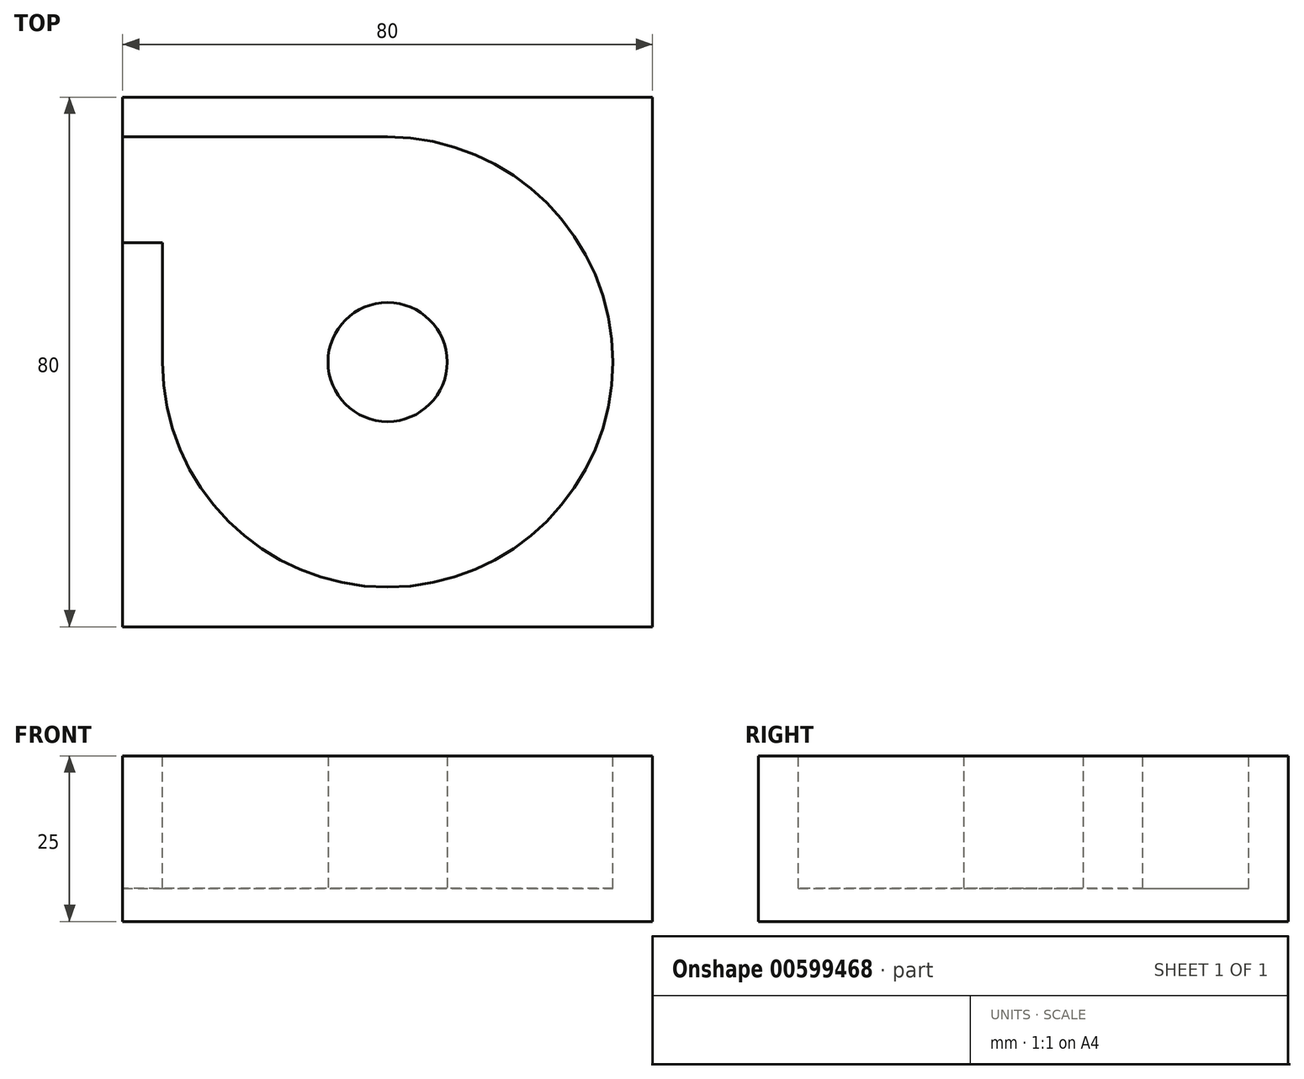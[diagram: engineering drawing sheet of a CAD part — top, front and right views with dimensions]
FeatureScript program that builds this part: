
annotation { "Feature Type Name" : "Feature", "Feature Type Description" : "" }
export const myFeature = defineFeature(function(context is Context, id is Id, definition is map)
    precondition{}
    {
        {
            var Q0;
            Q0=qCreatedBy(makeId("Top.planeOp"),FACE);
            var sketch = newSketch(context, id + "F0", { "sketchPlane" : qUnion([Q0])});
            skLineSegment(sketch, "E0.bottom", {"start": v(-40, 40) * mm, "end": v(40, 40) * mm});
            skLineSegment(sketch, "E0.top", {"start": v(-40, -40) * mm, "end": v(40, -40) * mm});
            skLineSegment(sketch, "E0.left", {"start": v(-40, 40) * mm, "end": v(-40, -40) * mm});
            skLineSegment(sketch, "E0.right", {"start": v(40, 40) * mm, "end": v(40, -40) * mm});
            skPoint(sketch, "E0.middle", {"position": v(0, 0) * mm});
            skSolve(sketch);
        }
        {
            var Q0;
            Q0 = qSketchRegion(id + "F0", true);
            extrude(context, id + "F1", {"entities" : qUnion([Q0]), "depth" : 25 * mm, "offsetDistance" : 25 * mm});
        }
        {
            var Q0;
            Q0=makeQuery(id+"F1.opExtrude","CAP_FACE",FACE,{"disambiguationData":[OSD([sQuery(id+"F0.wireOp",EDGE,"E0.bottom"),sQuery(id+"F0.wireOp",EDGE,"E0.top"),sQuery(id+"F0.wireOp",EDGE,"E0.left"),sQuery(id+"F0.wireOp",EDGE,"E0.right")])],"isStart":false});
            var sketch = newSketch(context, id + "F2", { "sketchPlane" : qUnion([Q0])});
            skCircle(sketch, "E1", {"center": v(0, 0) * mm, "radius": 34 * mm});
            skSolve(sketch);
        }
        {
            var Q0;
            Q0 = qSketchRegion(id + "F2", true);
            extrude(context, id + "F3", {"entities" : qUnion([Q0]), "operationType" : NewBodyOperationType.REMOVE, "oppositeDirection" : true, "depth" : 20 * mm, "offsetDistance" : 25 * mm});
        }
        {
            var Q0;
            Q0=makeQuery(id+"F3.boolean.opBoolean","COPY",FACE,{"derivedFrom":makeQuery(id+"F3.opExtrude","CAP_FACE",FACE,{"disambiguationData":[OSD([sQuery(id+"F2.wireOp",EDGE,"E1")])],"isStart":false})});
            var sketch = newSketch(context, id + "F4", { "sketchPlane" : qUnion([Q0])});
            skCircle(sketch, "E2", {"center": v(0, 0) * mm, "radius": 9 * mm});
            skSolve(sketch);
        }
        {
            var Q0;
            Q0 = qSketchRegion(id + "F4", true);
            extrude(context, id + "F5", {"entities" : qUnion([Q0]), "operationType" : NewBodyOperationType.ADD, "depth" : 20 * mm, "offsetDistance" : 25 * mm});
        }
        {
            var Q0;
            Q0=makeQuery(id+"F1.opExtrude","CAP_FACE",FACE,{"disambiguationData":[OSD([sQuery(id+"F0.wireOp",EDGE,"E0.bottom"),sQuery(id+"F0.wireOp",EDGE,"E0.top"),sQuery(id+"F0.wireOp",EDGE,"E0.left"),sQuery(id+"F0.wireOp",EDGE,"E0.right")])],"isStart":false});
            var sketch = newSketch(context, id + "F6", { "sketchPlane" : qUnion([Q0])});
            skLineSegment(sketch, "E3.bottom", {"start": v(-34, 0) * mm, "end": v(0, 0) * mm});
            skLineSegment(sketch, "E3.top", {"start": v(-34, 34) * mm, "end": v(0, 34) * mm});
            skLineSegment(sketch, "E3.left", {"start": v(-34, 0) * mm, "end": v(-34, 34) * mm});
            skLineSegment(sketch, "E3.right", {"start": v(0, 0) * mm, "end": v(0, 34) * mm});
            skSolve(sketch);
        }
        {
            var Q0;
            {var subQ0=sQuery(id+"F6.wireOp",EDGE,"E3.top");Q0=makeQuery(id+"F6.imprint","IMPRINT",FACE,{"disambiguationData":[TD([[makeQuery(id+"F6.imprint","IMPRINT",EDGE,{"derivedFrom":subQ0}),-1.0]])]});}
            var Q1;
            Q1=makeQuery(id+"F3.boolean.opBoolean","COPY",FACE,{"derivedFrom":makeQuery(id+"F3.opExtrude","CAP_FACE",FACE,{"disambiguationData":[OSD([sQuery(id+"F2.wireOp",EDGE,"E1")])],"isStart":false})});
            extrude(context, id + "F7", {"entities" : qUnion([Q0]), "operationType" : NewBodyOperationType.REMOVE, "endBound" : BoundingType.UP_TO_SURFACE, "oppositeDirection" : true, "depth" : 25 * mm, "endBoundEntityFace" : qUnion([Q1]), "offsetDistance" : 25 * mm});
        }
        {
            var Q0;
            Q0=makeQuery(id+"F1.opExtrude","CAP_FACE",FACE,{"disambiguationData":[OSD([sQuery(id+"F0.wireOp",EDGE,"E0.bottom"),sQuery(id+"F0.wireOp",EDGE,"E0.top"),sQuery(id+"F0.wireOp",EDGE,"E0.left"),sQuery(id+"F0.wireOp",EDGE,"E0.right")])],"isStart":false});
            var sketch = newSketch(context, id + "F8", { "sketchPlane" : qUnion([Q0])});
            skLineSegment(sketch, "E4.bottom", {"start": v(-34, 34) * mm, "end": v(-40, 34) * mm});
            skLineSegment(sketch, "E4.top", {"start": v(-34, 18) * mm, "end": v(-40, 18) * mm});
            skLineSegment(sketch, "E4.left", {"start": v(-34, 34) * mm, "end": v(-34, 18) * mm});
            skLineSegment(sketch, "E4.right", {"start": v(-40, 34) * mm, "end": v(-40, 18) * mm});
            skSolve(sketch);
        }
        {
            var Q0;
            Q0 = qSketchRegion(id + "F8", true);
            var Q1;
            {var subQ0=sQuery(id+"F2.wireOp",EDGE,"E1");Q1=makeQuery(id+"F7.boolean.opBoolean","MERGE",FACE,{"derivedFrom":[makeQuery(id+"F3.boolean.opBoolean","COPY",FACE,{"derivedFrom":makeQuery(id+"F3.opExtrude","CAP_FACE",FACE,{"disambiguationData":[OSD([subQ0])],"isStart":false})}),makeQuery(id+"F7.opExtrude","CAP_FACE",FACE,{"disambiguationData":[OSD([subQ0])],"isStart":false})]});}
            extrude(context, id + "F9", {"entities" : qUnion([Q0]), "operationType" : NewBodyOperationType.REMOVE, "endBound" : BoundingType.UP_TO_SURFACE, "oppositeDirection" : true, "depth" : 25 * mm, "endBoundEntityFace" : qUnion([Q1]), "offsetDistance" : 25 * mm});
        }
    });
